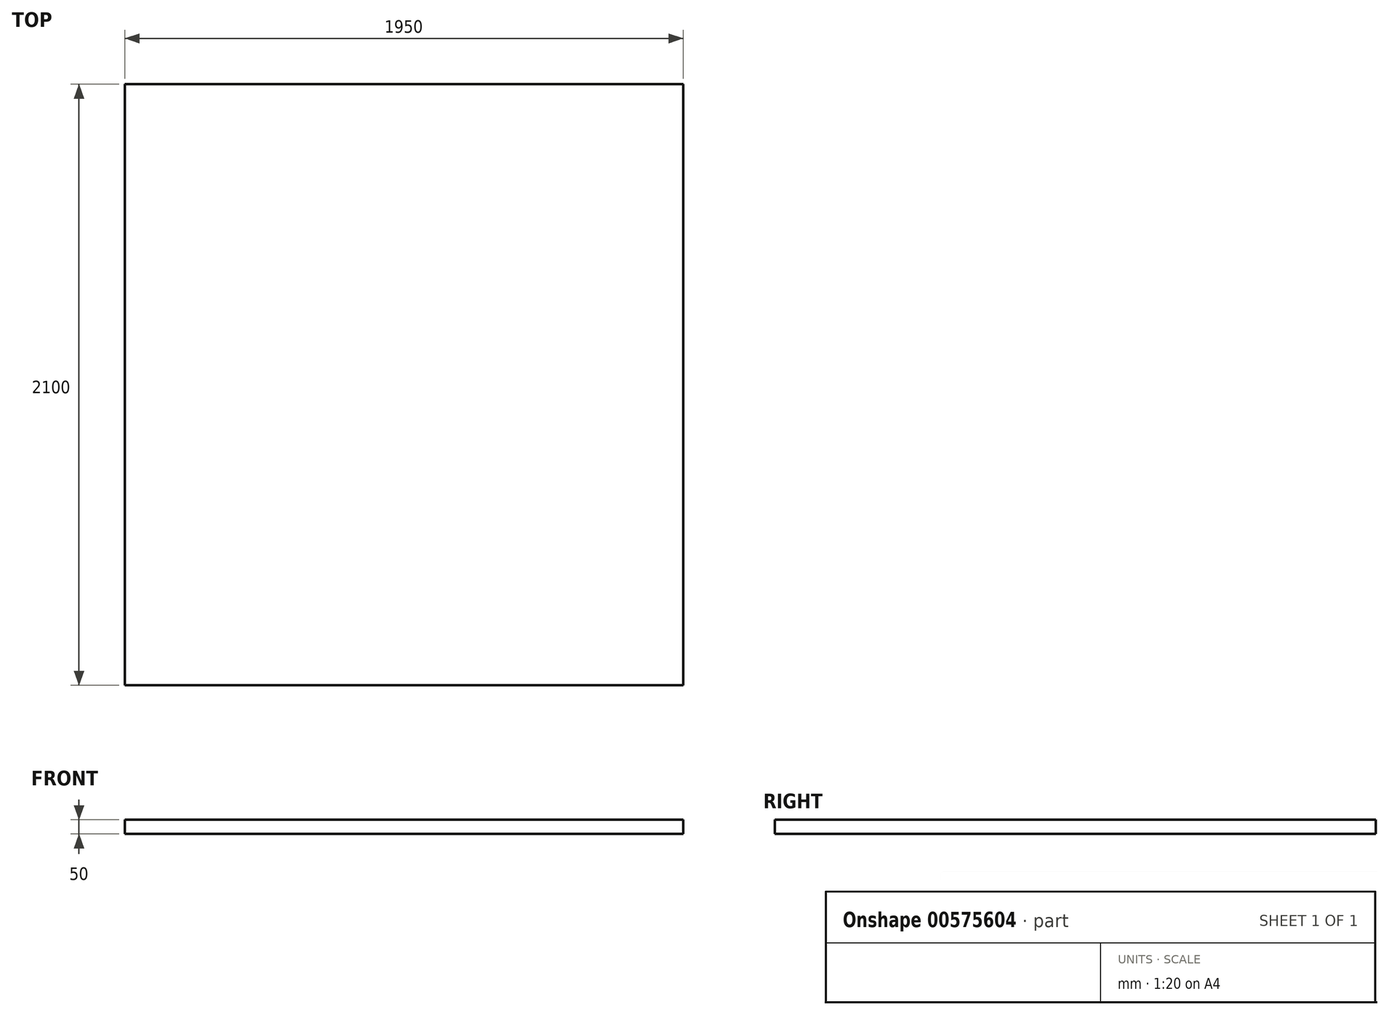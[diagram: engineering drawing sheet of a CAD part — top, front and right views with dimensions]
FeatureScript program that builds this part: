
annotation { "Feature Type Name" : "Feature", "Feature Type Description" : "" }
export const myFeature = defineFeature(function(context is Context, id is Id, definition is map)
    precondition{}
    {
        {
            var Q0;
            Q0=qCreatedBy(makeId("Top.planeOp"),FACE);
            var sketch = newSketch(context, id + "F0", { "sketchPlane" : qUnion([Q0])});
            skLineSegment(sketch, "E0.bottom", {"start": v(975, -1050) * mm, "end": v(-975, -1050) * mm});
            skLineSegment(sketch, "E0.top", {"start": v(975, 1050) * mm, "end": v(-975, 1050) * mm});
            skLineSegment(sketch, "E0.left", {"start": v(975, -1050) * mm, "end": v(975, 1050) * mm});
            skLineSegment(sketch, "E0.right", {"start": v(-975, -1050) * mm, "end": v(-975, 1050) * mm});
            skPoint(sketch, "E0.middle", {"position": v(0, 0) * mm});
            skSolve(sketch);
        }
        {
            var Q0;
            Q0 = qSketchRegion(id + "F0", true);
            extrude(context, id + "F1", {"entities" : qUnion([Q0]), "depth" : 50 * mm, "offsetDistance" : 25 * mm});
        }
    });
